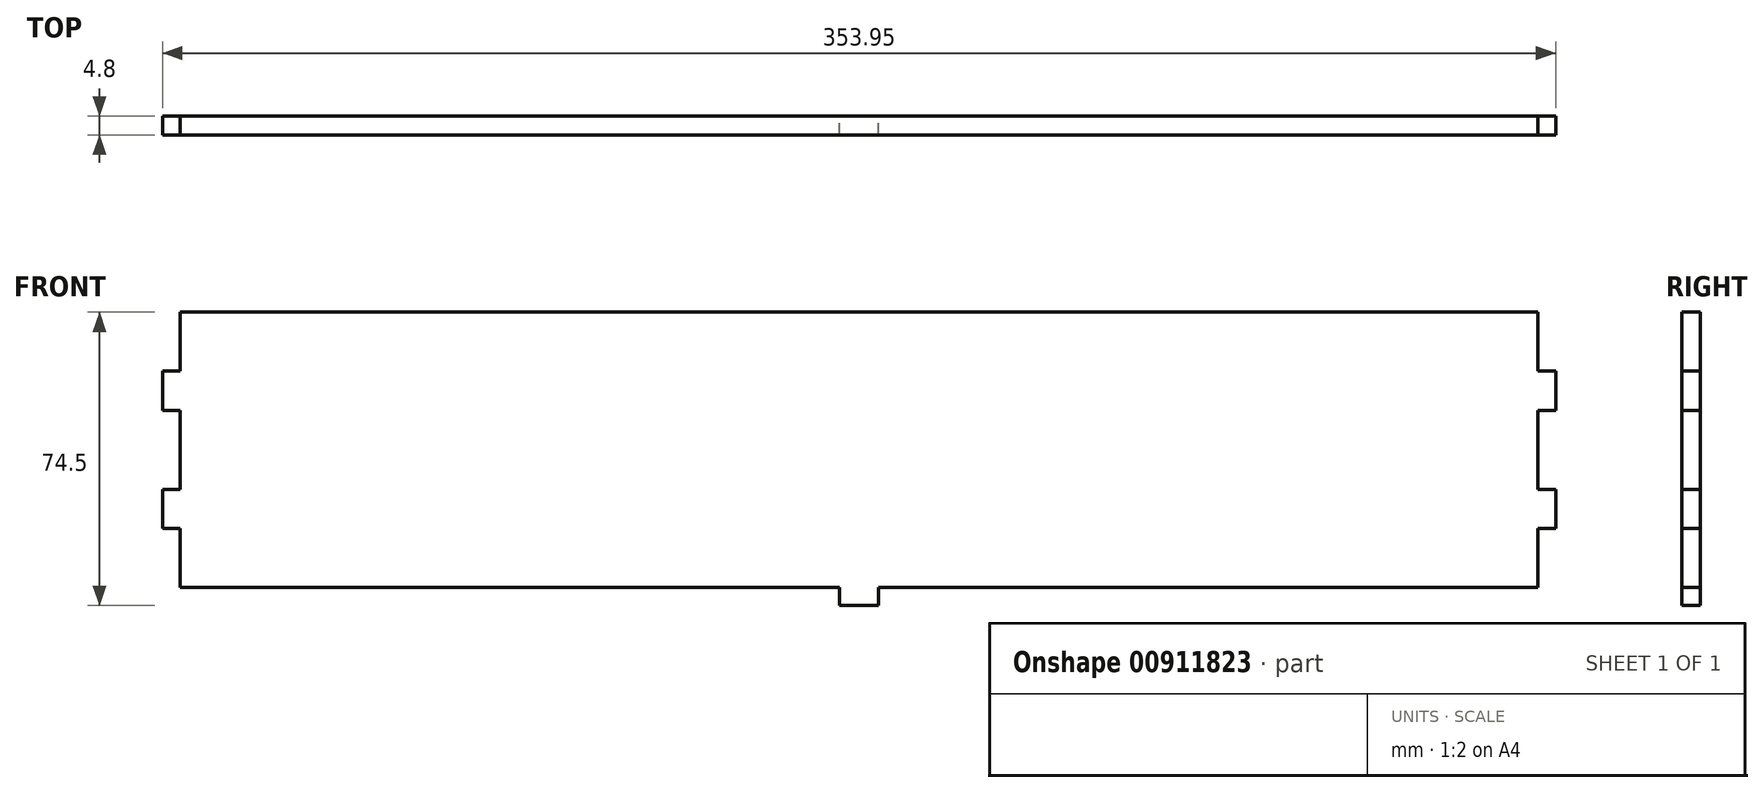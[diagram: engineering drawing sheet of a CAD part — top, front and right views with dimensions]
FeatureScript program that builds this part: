
annotation { "Feature Type Name" : "Feature", "Feature Type Description" : "" }
export const myFeature = defineFeature(function(context is Context, id is Id, definition is map)
    precondition{}
    {
        {
            var Q0;
            Q0=qCreatedBy(makeId("Front.planeOp"),FACE);
            var sketch = newSketch(context, id + "F0", { "sketchPlane" : qUnion([Q0])});
            skLineSegment(sketch, "E0", {"start": v(0, 0) * mm, "end": v(-344.95, 0) * mm});
            skLineSegment(sketch, "E1", {"start": v(-344.95, 0) * mm, "end": v(-344.95, 15) * mm});
            skLineSegment(sketch, "E2", {"start": v(-344.95, 70) * mm, "end": v(-182.28, 70) * mm});
            skLineSegment(sketch, "E3", {"start": v(0, 70) * mm, "end": v(0, 55) * mm});
            skLineSegment(sketch, "E4", {"start": v(-344.95, 70) * mm, "end": v(-344.95, 55) * mm});
            skLineSegment(sketch, "E5", {"start": v(-344.95, 55) * mm, "end": v(-349.45, 55) * mm});
            skLineSegment(sketch, "E6", {"start": v(-349.45, 55) * mm, "end": v(-349.45, 45) * mm});
            skLineSegment(sketch, "E7", {"start": v(-349.45, 45) * mm, "end": v(-344.95, 45) * mm});
            skLineSegment(sketch, "E8.MirrorCS", {"start": v(-349.45, 25) * mm, "end": v(-344.95, 25) * mm});
            skLineSegment(sketch, "E9.MirrorCS", {"start": v(-344.95, 15) * mm, "end": v(-349.45, 15) * mm});
            skLineSegment(sketch, "E10.MirrorCS", {"start": v(4.5, 45) * mm, "end": v(0, 45) * mm});
            skLineSegment(sketch, "E11.MirrorCS", {"start": v(0, 55) * mm, "end": v(4.5, 55) * mm});
            skLineSegment(sketch, "E12.MirrorCS", {"start": v(4.5, 25) * mm, "end": v(0, 25) * mm});
            skLineSegment(sketch, "E13.MirrorCS", {"start": v(0, 15) * mm, "end": v(4.5, 15) * mm});
            skLineSegment(sketch, "E14.trimOffspring", {"start": v(0, 45) * mm, "end": v(0, 25) * mm});
            skLineSegment(sketch, "E15.trimOffspring", {"start": v(0, 15) * mm, "end": v(0, 0) * mm});
            skLineSegment(sketch, "E16.trimOffspring", {"start": v(-344.95, 55) * mm, "end": v(-344.95, 70) * mm});
            skLineSegment(sketch, "E17.trimOffspring", {"start": v(-344.95, 25) * mm, "end": v(-344.95, 45) * mm});
            skLineSegment(sketch, "E18.trimOffspring", {"start": v(-172.28, 70) * mm, "end": v(0, 70) * mm});
            skLineSegment(sketch, "E19", {"start": v(-349.45, 25) * mm, "end": v(-349.45, 15) * mm});
            skLineSegment(sketch, "E20.MirrorCS", {"start": v(-167.48, -0.23) * mm, "end": v(-167.48, -4.5) * mm});
            skLineSegment(sketch, "E21.MirrorCS", {"start": v(-177.48, 0) * mm, "end": v(-177.48, -4.5) * mm});
            skLineSegment(sketch, "E22", {"start": v(-182.28, 70) * mm, "end": v(-172.28, 70) * mm});
            skLineSegment(sketch, "E23", {"start": v(-344.95, 25) * mm, "end": v(-349.45, 25) * mm});
            skLineSegment(sketch, "E24", {"start": v(-349.45, 15) * mm, "end": v(-344.95, 15) * mm});
            skLineSegment(sketch, "E25", {"start": v(-344.95, 25) * mm, "end": v(-344.95, 15) * mm});
            skLineSegment(sketch, "E26", {"start": v(4.5, 25) * mm, "end": v(4.5, 15) * mm});
            skPoint(sketch, "E27.orphan", {"position": v(4.8, 15) * mm});
            skLineSegment(sketch, "E28", {"start": v(4.5, 55) * mm, "end": v(4.5, 45) * mm});
            skPoint(sketch, "E29.orphan", {"position": v(4.8, 45) * mm});
            skLineSegment(sketch, "E30", {"start": v(-177.48, -4.5) * mm, "end": v(-167.48, -4.5) * mm});
            skLineSegment(sketch, "E31", {"start": v(-167.48, 0) * mm, "end": v(-167.48, -0.23) * mm});
            skSolve(sketch);
        }
        {
            var Q0;
            Q0=makeQuery(id+"F0.imprint","IMPRINT",FACE,{"disambiguationData":[TD([[makeQuery(id+"F0.imprint","IMPRINT",EDGE,{"derivedFrom":sQuery(id+"F0.wireOp",EDGE,"E0")}),-1.0]])]});
            var Q1;
            {var subQ0=sQuery(id+"F0.wireOp",EDGE,"cyidqIZi-dBYG-pd5h-6GGm-RbbqEJob11CW");Q1=makeQuery(id+"F0.imprint","IMPRINT",FACE,{"disambiguationData":[TD([[makeQuery(id+"F0.imprint","IMPRINT",EDGE,{"derivedFrom":subQ0}),-1.0]])]});}
            var Q2;
            {var subQ6=sQuery(id+"F0.wireOp",EDGE,"a64813e8-a9ca-476d-a873-92c8efeca17a0.MirrorCS");Q2=makeQuery(id+"F0.imprint","IMPRINT",FACE,{"disambiguationData":[TD([[makeQuery(id+"F0.imprint","IMPRINT",EDGE,{"derivedFrom":subQ6}),1.0]])]});}
            var Q3;
            {var subQ0=sQuery(id+"F0.wireOp",EDGE,"E20.MirrorCS");Q3=makeQuery(id+"F0.imprint","IMPRINT",FACE,{"disambiguationData":[TD([[makeQuery(id+"F0.imprint","IMPRINT",EDGE,{"derivedFrom":subQ0}),-1.0]])]});}
            var Q4;
            Q4=makeQuery(id+"F0.imprint","IMPRINT",FACE,{"disambiguationData":[TD([[makeQuery(id+"F0.imprint","IMPRINT",EDGE,{"derivedFrom":sQuery(id+"F0.wireOp",EDGE,"E19")}),1.0]])]});
            extrude(context, id + "F1", {"entities" : qUnion([Q0, Q1, Q2, Q3, Q4]), "depth" : 4.8 * mm, "offsetDistance" : 25 * mm});
        }
    });
